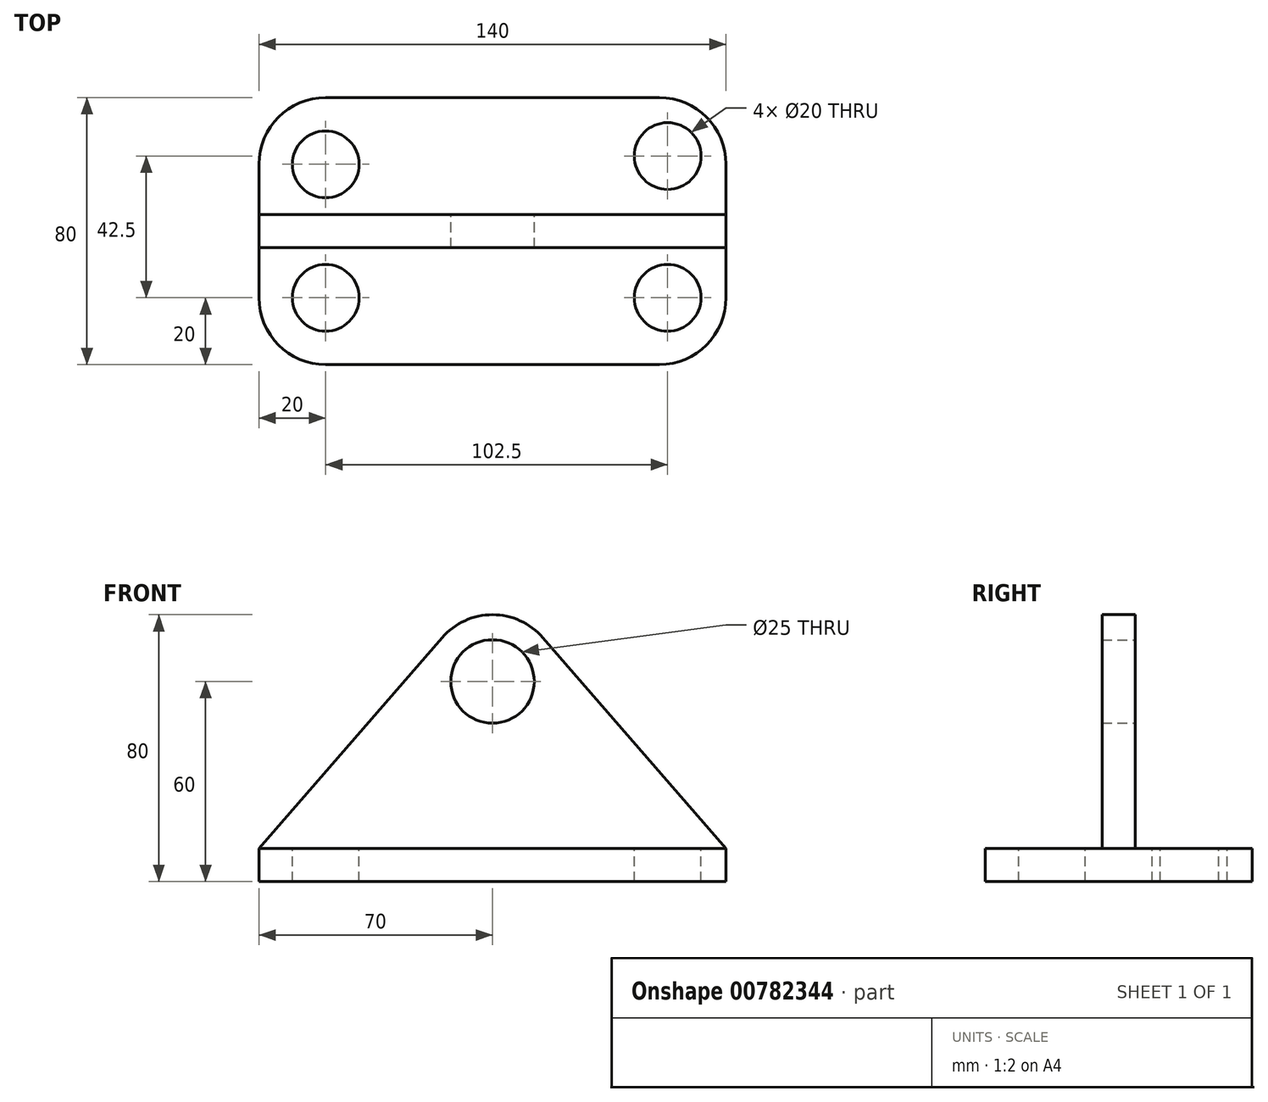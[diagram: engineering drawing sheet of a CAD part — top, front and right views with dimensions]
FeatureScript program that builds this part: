
annotation { "Feature Type Name" : "Feature", "Feature Type Description" : "" }
export const myFeature = defineFeature(function(context is Context, id is Id, definition is map)
    precondition{}
    {
        {
            var Q0;
            Q0=qCreatedBy(makeId("Front.planeOp"),FACE);
            var sketch = newSketch(context, id + "F0", { "sketchPlane" : qUnion([Q0])});
            skLineSegment(sketch, "E0.bottom", {"start": v(70, -5) * mm, "end": v(-70, -5) * mm});
            skLineSegment(sketch, "E0.top", {"start": v(70, 5) * mm, "end": v(-70, 5) * mm});
            skLineSegment(sketch, "E0.left", {"start": v(70, -5) * mm, "end": v(70, 5) * mm});
            skLineSegment(sketch, "E0.right", {"start": v(-70, -5) * mm, "end": v(-70, 5) * mm});
            skPoint(sketch, "E0.middle", {"position": v(0, 0) * mm});
            skLineSegment(sketch, "E1", {"start": v(0, -5) * mm, "end": v(0, 55) * mm, "construction": true});
            skArc(sketch, "E2", {"start": v(15.1, 68.13) * mm, "mid": v(0, 75) * mm, "end": v(-15.1, 68.13) * mm});
            skCircle(sketch, "E3", {"center": v(0, 55) * mm, "radius": 12.5 * mm});
            skLineSegment(sketch, "E4", {"start": v(-70, 5) * mm, "end": v(-15.1, 68.13) * mm});
            skLineSegment(sketch, "E5", {"start": v(70, 5) * mm, "end": v(15.1, 68.13) * mm});
            skSolve(sketch);
        }
        {
            var Q0;
            Q0=makeQuery(id+"F0.imprint","IMPRINT",FACE,{"disambiguationData":[TD([[makeQuery(id+"F0.imprint","IMPRINT",EDGE,{"derivedFrom":sQuery(id+"F0.wireOp",EDGE,"E0.bottom")}),-1.0]])]});
            extrude(context, id + "F1", {"entities" : qUnion([Q0]), "endBound" : BoundingType.SYMMETRIC, "depth" : 80 * mm, "offsetDistance" : 25.4 * mm});
        }
        {
            var Q0;
            Q0 = qSketchRegion(id + "F0", true);
            extrude(context, id + "F2", {"entities" : qUnion([Q0]), "operationType" : NewBodyOperationType.ADD, "endBound" : BoundingType.SYMMETRIC, "depth" : 10 * mm, "offsetDistance" : 25.4 * mm});
        }
        {
            var Q0;
            Q0=makeQuery(id+"F1.opExtrude","CAP_EDGE",EDGE,{"disambiguationData":[OSD([sQuery(id+"F0.wireOp",EDGE,"E0.right")])],"isStart":true});
            var Q1;
            Q1=makeQuery(id+"F1.opExtrude","CAP_EDGE",EDGE,{"disambiguationData":[OSD([sQuery(id+"F0.wireOp",EDGE,"E0.right")])],"isStart":false});
            var Q2;
            Q2=makeQuery(id+"F1.opExtrude","CAP_EDGE",EDGE,{"disambiguationData":[OSD([sQuery(id+"F0.wireOp",EDGE,"E0.left")])],"isStart":true});
            var Q3;
            Q3=makeQuery(id+"F1.opExtrude","CAP_EDGE",EDGE,{"disambiguationData":[OSD([sQuery(id+"F0.wireOp",EDGE,"E0.left")])],"isStart":false});
            fillet(context, id + "F3", {"entities" : qUnion([Q0, Q1, Q2, Q3]), "radius" : 20 * mm, "tangentPropagation" : true, "allowEdgeOverflow" : false});
        }
        {
            var Q0;
            Q0=qCreatedBy(makeId("Top.planeOp"),FACE);
            var sketch = newSketch(context, id + "F4", { "sketchPlane" : qUnion([Q0])});
            skPoint(sketch, "E6", {"position": v(52.5, 22.5) * mm});
            skCircle(sketch, "E7", {"center": v(52.5, 22.5) * mm, "radius": 10 * mm});
            skPoint(sketch, "E8", {"position": v(-50, 20) * mm});
            skCircle(sketch, "E9", {"center": v(-50, 20) * mm, "radius": 10 * mm});
            skPoint(sketch, "E10", {"position": v(-50, -20) * mm});
            skPoint(sketch, "E11", {"position": v(52.5, -20) * mm});
            skCircle(sketch, "E12", {"center": v(-50, -20) * mm, "radius": 10 * mm});
            skCircle(sketch, "E13", {"center": v(52.5, -20) * mm, "radius": 10 * mm});
            skSolve(sketch);
        }
        {
            var Q0;
            Q0=sQuery(id+"F4.wireOp",VERTEX,"E6");
            var Q1;
            Q1=makeQuery(id+"F1.opExtrude","SWEPT_BODY",BODY,{"disambiguationData":[OSD([sQuery(id+"F0.wireOp",EDGE,"E0.bottom"),sQuery(id+"F0.wireOp",EDGE,"E0.top"),sQuery(id+"F0.wireOp",EDGE,"E0.left"),sQuery(id+"F0.wireOp",EDGE,"E0.right")])]});
            hole(context, id + "F5", {"style" : HoleStyle.SIMPLE, "endStyle" : HoleEndStyle.THROUGH, "holeDiameter" : 20 * mm, "majorDiameter" : 6.35 * mm, "isTappedThrough" : true, "tappedDepth" : 12.7 * mm, "tapClearance" : 3, "locations" : qUnion([Q0]), "scope" : qUnion([Q1])});
        }
        {
            var Q0;
            Q0=sQuery(id+"F4.wireOp",VERTEX,"E6");
            var Q1;
            Q1=makeQuery(id+"F1.opExtrude","SWEPT_BODY",BODY,{"disambiguationData":[OSD([sQuery(id+"F0.wireOp",EDGE,"E0.bottom"),sQuery(id+"F0.wireOp",EDGE,"E0.top"),sQuery(id+"F0.wireOp",EDGE,"E0.left"),sQuery(id+"F0.wireOp",EDGE,"E0.right")])]});
            hole(context, id + "F6", {"style" : HoleStyle.SIMPLE, "endStyle" : HoleEndStyle.THROUGH, "oppositeDirection" : true, "holeDiameter" : 20 * mm, "majorDiameter" : 6.35 * mm, "isTappedThrough" : true, "tappedDepth" : 12.7 * mm, "tapClearance" : 3, "locations" : qUnion([Q0]), "scope" : qUnion([Q1])});
        }
        {
            var Q0;
            Q0=sQuery(id+"F4.wireOp",VERTEX,"E8");
            var Q1;
            Q1=makeQuery(id+"F1.opExtrude","SWEPT_BODY",BODY,{"disambiguationData":[OSD([sQuery(id+"F0.wireOp",EDGE,"E0.bottom"),sQuery(id+"F0.wireOp",EDGE,"E0.top"),sQuery(id+"F0.wireOp",EDGE,"E0.left"),sQuery(id+"F0.wireOp",EDGE,"E0.right")])]});
            hole(context, id + "F7", {"style" : HoleStyle.SIMPLE, "endStyle" : HoleEndStyle.THROUGH, "holeDiameter" : 20 * mm, "majorDiameter" : 6.35 * mm, "isTappedThrough" : true, "tappedDepth" : 12.7 * mm, "tapClearance" : 3, "locations" : qUnion([Q0]), "scope" : qUnion([Q1])});
        }
        {
            var Q0;
            Q0=sQuery(id+"F4.wireOp",VERTEX,"E8");
            var Q1;
            Q1=makeQuery(id+"F1.opExtrude","SWEPT_BODY",BODY,{"disambiguationData":[OSD([sQuery(id+"F0.wireOp",EDGE,"E0.bottom"),sQuery(id+"F0.wireOp",EDGE,"E0.top"),sQuery(id+"F0.wireOp",EDGE,"E0.left"),sQuery(id+"F0.wireOp",EDGE,"E0.right")])]});
            hole(context, id + "F8", {"style" : HoleStyle.SIMPLE, "endStyle" : HoleEndStyle.THROUGH, "oppositeDirection" : true, "holeDiameter" : 20 * mm, "majorDiameter" : 6.35 * mm, "isTappedThrough" : true, "tappedDepth" : 12.7 * mm, "tapClearance" : 3, "locations" : qUnion([Q0]), "scope" : qUnion([Q1])});
        }
        {
            var Q0;
            Q0=sQuery(id+"F4.wireOp",VERTEX,"E10");
            var Q1;
            Q1=sQuery(id+"F4.wireOp",VERTEX,"E11");
            var Q2;
            Q2=makeQuery(id+"F1.opExtrude","SWEPT_BODY",BODY,{"disambiguationData":[OSD([sQuery(id+"F0.wireOp",EDGE,"E0.bottom"),sQuery(id+"F0.wireOp",EDGE,"E0.top"),sQuery(id+"F0.wireOp",EDGE,"E0.left"),sQuery(id+"F0.wireOp",EDGE,"E0.right")])]});
            hole(context, id + "F9", {"style" : HoleStyle.SIMPLE, "endStyle" : HoleEndStyle.THROUGH, "holeDiameter" : 20 * mm, "majorDiameter" : 6.35 * mm, "isTappedThrough" : true, "tappedDepth" : 12.7 * mm, "tapClearance" : 3, "locations" : qUnion([Q0, Q1]), "scope" : qUnion([Q2])});
        }
        {
            var Q0;
            Q0=sQuery(id+"F4.wireOp",VERTEX,"E10");
            var Q1;
            Q1=sQuery(id+"F4.wireOp",VERTEX,"E11");
            var Q2;
            Q2=makeQuery(id+"F1.opExtrude","SWEPT_BODY",BODY,{"disambiguationData":[OSD([sQuery(id+"F0.wireOp",EDGE,"E0.bottom"),sQuery(id+"F0.wireOp",EDGE,"E0.top"),sQuery(id+"F0.wireOp",EDGE,"E0.left"),sQuery(id+"F0.wireOp",EDGE,"E0.right")])]});
            hole(context, id + "F10", {"style" : HoleStyle.SIMPLE, "endStyle" : HoleEndStyle.THROUGH, "oppositeDirection" : true, "holeDiameter" : 20 * mm, "majorDiameter" : 6.35 * mm, "isTappedThrough" : true, "tappedDepth" : 12.7 * mm, "tapClearance" : 3, "locations" : qUnion([Q0, Q1]), "scope" : qUnion([Q2])});
        }
    });
